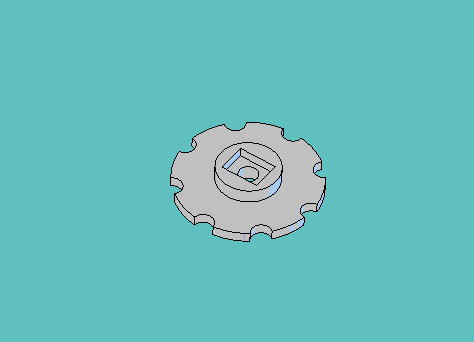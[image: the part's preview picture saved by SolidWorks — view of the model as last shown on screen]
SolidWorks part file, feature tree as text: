
SOLIDWORKS PART (.sldprt)
format: sldprt  version: not decoded by parser v0  size: 673,280 bytes
history: native  units: mm
features: sketch x4, extrude x2, cut_extrude x2, material x1 (+11 scaffold rows collapsed)
feature tree (20):
  scaffold x11  (default folders/planes/origin — collapsed)
  material  "Material <not specified>"
  sketch  "Sketch1"  dims[c1.D3=50.292mm c1.D4=~6.746875mm c1.D5=~6.746875mm c1.D6=~6.746875mm c1.D7=~6.746875mm c1.D8=~6.746875mm c1.D9=~6.746875mm c1.D10=~6.746875mm c1.D11=~6.746875mm c1.D12=56.8198mm c2.D3=6.35mm c2.D1=~130.783491mm c3.D1=45.0deg c3.D2=~130.181673mm c4.D2=45.0deg c4.D13=3.429mm c4.D12=0.254mm c4.D3=26.9875mm]
  extrude  "Extrude1"  Depth=2.89052mm
  sketch  "Sketch5"  dims[D1=20.32mm]
  extrude  "Extrude2"  Depth=6.35mm
  sketch  "Sketch3"  dims[D1=6.35mm D2=0.254mm]
  cut_extrude  "Cut-Extrude1"  [1 undecoded]
  sketch  "Sketch6"  dims[D1=12.954mm D2=9.779mm D3=6.477mm D4=4.8895mm]
  cut_extrude  "Cut-Extrude2"  Depth=4.7625mm
decode coverage: 7 of 8 modeling features carry decoded parameters
note: ~ marks probable driven/reference dimensions
note: 1 parameter value undecoded
note: suppression state not decoded; provenance and decode notes live in map.json
